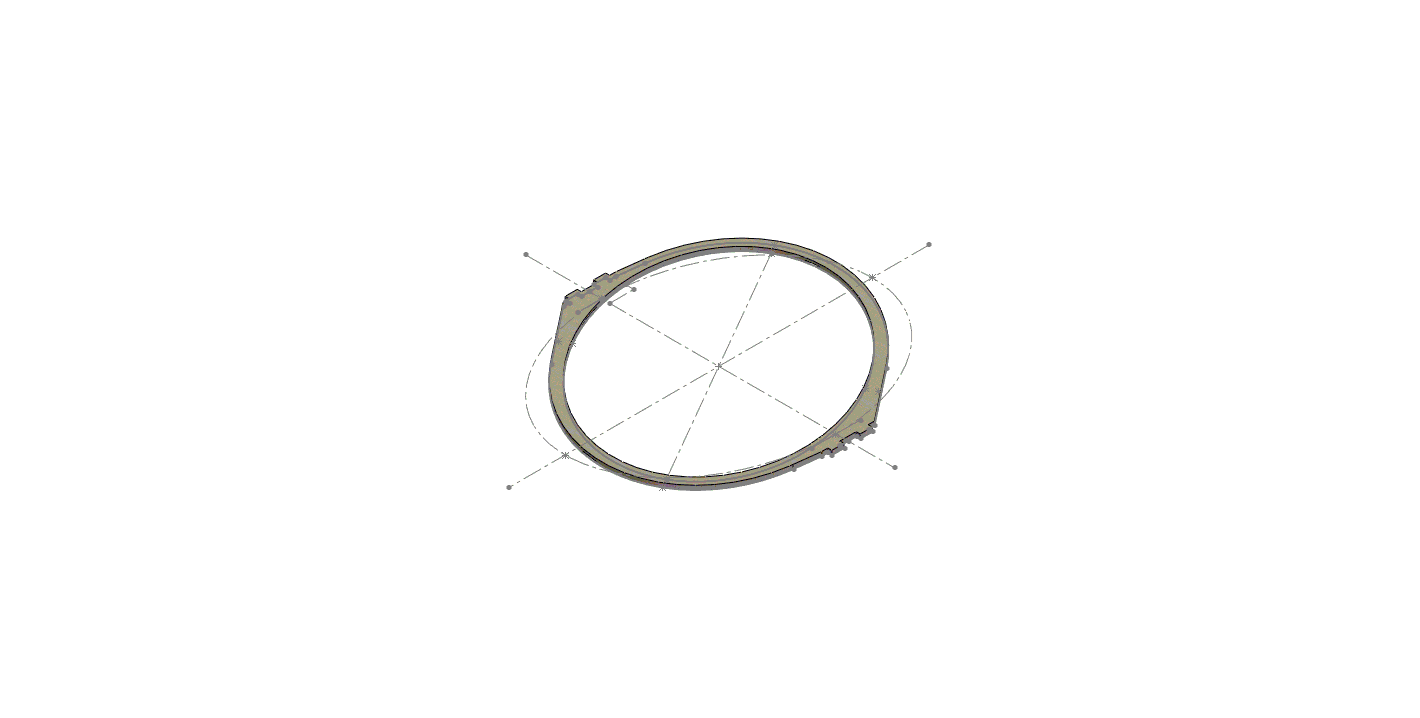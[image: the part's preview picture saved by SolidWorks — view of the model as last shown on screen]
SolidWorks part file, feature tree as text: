
SOLIDWORKS PART (.sldprt)
format: sldprt  version: not decoded by parser v0  size: 248,832 bytes
history: native  units: mm
features: sketch x4, cut_extrude x3, material x1, extrude x1 (+12 scaffold rows collapsed)
feature tree (21):
  scaffold x12  (default folders/planes/origin — collapsed)
  material  "Material <not specified>"
  sketch  "Sketch1"  dims[c1.D1=530.0mm c1.D2=710.0mm c1.D3=580.0mm c1.D4=760.0mm c1.D5=20.0mm c1.D6=260.0mm c1.D7=60.0mm c2.D6=30.0mm c2.D8=10.0mm c2.D9=10.0mm c2.D10=~709.886148mm c3.D10=30.0deg c3.D11=710.0mm c3.D12=530.0mm c3.D13=760.0mm c3.D14=580.0mm c3.D2=10.0mm c3.D6=10.0mm c3.D8=10.0mm c3.D9=320.0mm c3.D15=30.0mm c3.D16=30.0mm c3.D17=20.0mm c3.D18=20.0mm c3.D19=15.0mm c3.D20=15.0mm c4.D9=~78.52642deg]
  extrude  "Boss-Extrude1"  Depth=10mm
  sketch  "Sketch2"  dims[D1=10.0mm D2=10.0mm]
  cut_extrude  "Cut-Extrude1"  Depth=4mm
  sketch  "Sketch4"  dims[D1=5.0mm]
  cut_extrude  "Cut-Extrude4"  Depth=10mm
  sketch  "Sketch5"  dims[D1=5.0mm]
  cut_extrude  "Cut-Extrude5"  Depth=10mm
decode coverage: 8 of 8 modeling features carry decoded parameters
note: ~ marks probable driven/reference dimensions
note: suppression state not decoded; provenance and decode notes live in map.json
